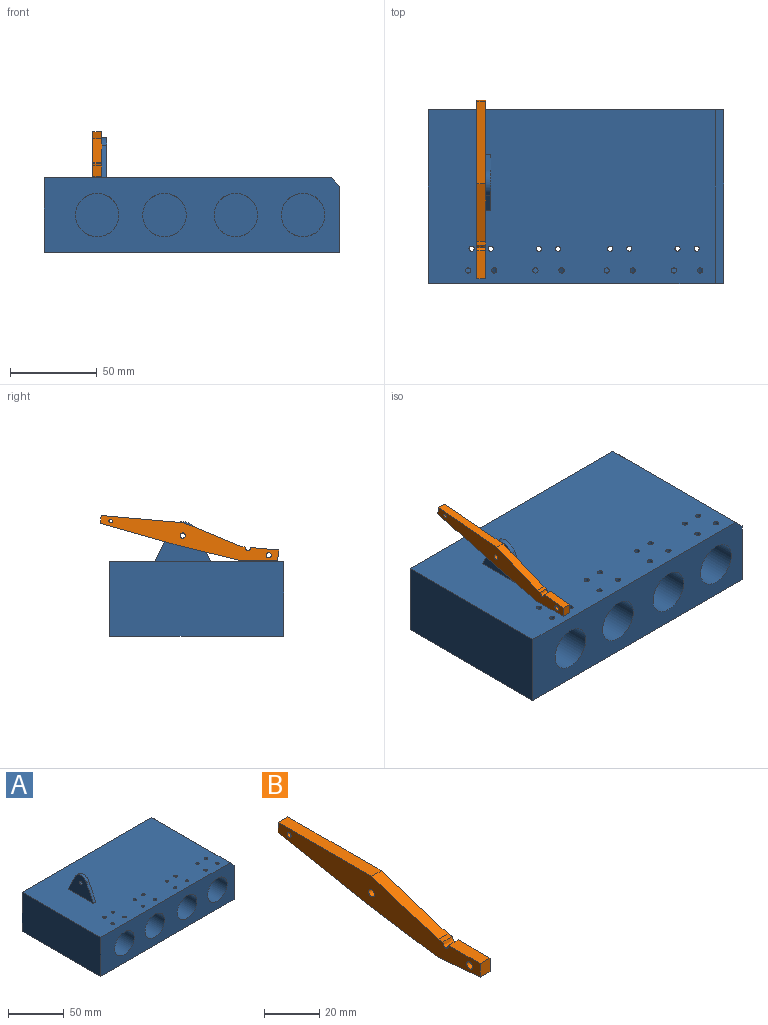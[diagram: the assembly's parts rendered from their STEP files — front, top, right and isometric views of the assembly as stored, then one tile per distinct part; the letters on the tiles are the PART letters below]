
ASSEMBLY  parts=2 mates=1
PART A: 45 faces, bbox 170x100x66 mm
  f0: plane 18.44x8.78mm, normal (0,-0.9,0.43), area 61.3mm2, adj f2,f4,f5,f10
  f1: plane 18.44x8.78mm, normal (0,0.9,0.43), area 61.3mm2, adj f2,f4,f5,f10
  f2: cylinder r=8mm len=14.45mm, axis (-1,0,0), area 54.1mm2, adj f0,f1,f4,f5
  f3: cylinder r=1.5mm len=3mm, axis (-1,0,0), area 28.3mm2, adj f4,f5
  f4: plane 32x23mm, normal (1,0,0), area 468.4mm2, adj f0,f1,f2,f3,f10
  f5: plane 32x23mm, normal (-1,0,0), area 468.4mm2, adj f0,f1,f2,f3,f10
  f6: plane 170x43mm, normal (0,-1,0), area 5334mm2, adj f7,f9,f10,f11,f12,f14,f16,f18
  f7: plane 100x38mm, normal (1,0,0), area 3800mm2, adj f6,f8,f11,f20
  f8: plane 170x43mm, normal (0,1,0), area 7297.5mm2, adj f7,f9,f10,f11,f20
  f9: plane 100x43mm, normal (-1,0,0), area 4300mm2, adj f6,f8,f10,f11
  f10: plane 165x100mm, normal (0,0,1), area 16290.9mm2, adj f0,f1,f4,f5,f6,f8,f9,f20
  f11: plane 170x100mm, normal (0,0,-1), area 16943.5mm2, adj f6,f7,f8,f9,f22,f24,f26,f28
  f12: cylinder r=12.5mm len=40mm, axis (0,-1,0), area 3092.2mm2, adj f6,f13,f33,f34,f35,f36,f43,f44
  f13: plane 25x25mm, normal (0,-1,0), area 490.9mm2, adj f12
  f14: cylinder r=12.5mm len=40mm, axis (0,-1,0), area 3092.2mm2, adj f6,f15,f29,f30,f31,f32,f41,f42
  f15: plane 25x25mm, normal (0,-1,0), area 490.9mm2, adj f14
  f16: cylinder r=12.5mm len=40mm, axis (0,-1,0), area 3092.2mm2, adj f6,f17,f25,f26,f27,f28,f39,f40
  f17: plane 25x25mm, normal (0,-1,0), area 490.9mm2, adj f16
  f18: cylinder r=12.5mm len=40mm, axis (0,-1,0), area 3092.2mm2, adj f6,f19,f21,f22,f23,f24,f37,f38
  f19: plane 25x25mm, normal (0,-1,0), area 490.9mm2, adj f18
  f20: plane 100x5mm, normal (0.71,0,0.71), area 707.1mm2, adj f6,f7,f8,f10
  f21: cylinder r=1.5mm len=11.14mm, axis (0,0,1), area 97.4mm2, adj f10,f18
  f22: cylinder r=1.5mm len=11.14mm, axis (0,0,1), area 97.4mm2, adj f11,f18
  f23: cylinder r=1.5mm len=11.14mm, axis (0,0,1), area 97.4mm2, adj f10,f18
  f24: cylinder r=1.5mm len=11.14mm, axis (0,0,1), area 97.4mm2, adj f11,f18
  f25: cylinder r=1.5mm len=11.14mm, axis (0,0,1), area 97.4mm2, adj f10,f16
  f26: cylinder r=1.5mm len=11.14mm, axis (0,0,1), area 97.4mm2, adj f11,f16
  f27: cylinder r=1.5mm len=11.14mm, axis (0,0,1), area 97.4mm2, adj f10,f16
  f28: cylinder r=1.5mm len=11.14mm, axis (0,0,1), area 97.4mm2, adj f11,f16
  f29: cylinder r=1.5mm len=11.14mm, axis (0,0,1), area 97.4mm2, adj f10,f14
  f30: cylinder r=1.5mm len=11.14mm, axis (0,0,1), area 97.4mm2, adj f11,f14
  f31: cylinder r=1.5mm len=11.14mm, axis (0,0,1), area 97.4mm2, adj f10,f14
  f32: cylinder r=1.5mm len=11.14mm, axis (0,0,1), area 97.4mm2, adj f11,f14
  f33: cylinder r=1.5mm len=11.14mm, axis (0,0,1), area 97.4mm2, adj f10,f12
  f34: cylinder r=1.5mm len=11.14mm, axis (0,0,1), area 97.4mm2, adj f11,f12
  f35: cylinder r=1.5mm len=11.14mm, axis (0,0,1), area 97.4mm2, adj f10,f12
  f36: cylinder r=1.5mm len=11.14mm, axis (0,0,1), area 97.4mm2, adj f11,f12
  f37: cylinder r=1.5mm len=12.83mm, axis (0,0,1), area 109.2mm2, adj f10,f18
  f38: cylinder r=1.5mm len=12.83mm, axis (0,0,1), area 109.2mm2, adj f10,f18
  f39: cylinder r=1.5mm len=12.83mm, axis (0,0,1), area 109.2mm2, adj f10,f16
  f40: cylinder r=1.5mm len=12.83mm, axis (0,0,1), area 109.2mm2, adj f10,f16
  f41: cylinder r=1.5mm len=12.83mm, axis (0,0,1), area 109.2mm2, adj f10,f14
  f42: cylinder r=1.5mm len=12.83mm, axis (0,0,1), area 109.2mm2, adj f10,f14
  f43: cylinder r=1.5mm len=12.83mm, axis (0,0,1), area 109.2mm2, adj f10,f12
  f44: cylinder r=1.5mm len=12.83mm, axis (0,0,1), area 109.2mm2, adj f10,f12
PART B: 16 faces, bbox 5x103.4x18.8 mm
  f0: plane 16.17x5mm, normal (0,0,1), area 80.8mm2, adj f1,f13,f14,f15
  f1: extruded ~5x2mm, area 13.4mm2, adj f0,f2,f14,f15
  f2: extruded ~5x2mm, area 13.4mm2, adj f1,f3,f14,f15
  f3: plane 5x2.27mm, normal (0,0,1), area 11.3mm2, adj f2,f4,f14,f15
  f4: plane 34.15x10.84mm, normal (0,-0.3,0.95), area 179.2mm2, adj f3,f5,f14,f15
  f5: plane 47.78x5mm, normal (0,0,1), area 238.9mm2, adj f4,f6,f14,f15
  f6: plane 5x4.53mm, normal (0,1,0), area 22.6mm2, adj f5,f7,f14,f15
  f7: plane 46.72x8.96mm, normal (0,0.19,-0.98), area 237.8mm2, adj f6,f8,f14,f15
  f8: plane 35.18x5.32mm, normal (0,0.15,-0.99), area 177.9mm2, adj f7,f9,f14,f15
  f9: plane 21.47x5mm, normal (0,-0.09,-1), area 107.8mm2, adj f8,f13,f14,f15
  f10: cylinder r=1.5mm len=5mm, axis (1,0,0), area 47.1mm2, adj f14,f15
  f11: cylinder r=1.5mm len=5mm, axis (1,0,0), area 47.1mm2, adj f14,f15
  f12: cylinder r=1mm len=5mm, axis (1,0,0), area 31.4mm2, adj f14,f15
  f13: plane 6x5mm, normal (0,-1,0), area 30mm2, adj f0,f9,f14,f15
  f14: plane 103.37x18.81mm, normal (-1,0,0), area 932.7mm2, adj f0,f1,f2,f3,f4,f5,f6,f7
  f15: plane 103.37x18.81mm, normal (1,0,0), area 932.7mm2, adj f0,f1,f2,f3,f4,f5,f6,f7
PLACE A t=(-28.79,21.64,9.27)mm fixed
PLACE B rot(axis=(1,0,0),5deg) t=(-28.79,26.72,8.8)mm
MATE revolute A.f2 <-> B.f11  axis (1,0,0) through (-85.83,29.56,67.27)mm
